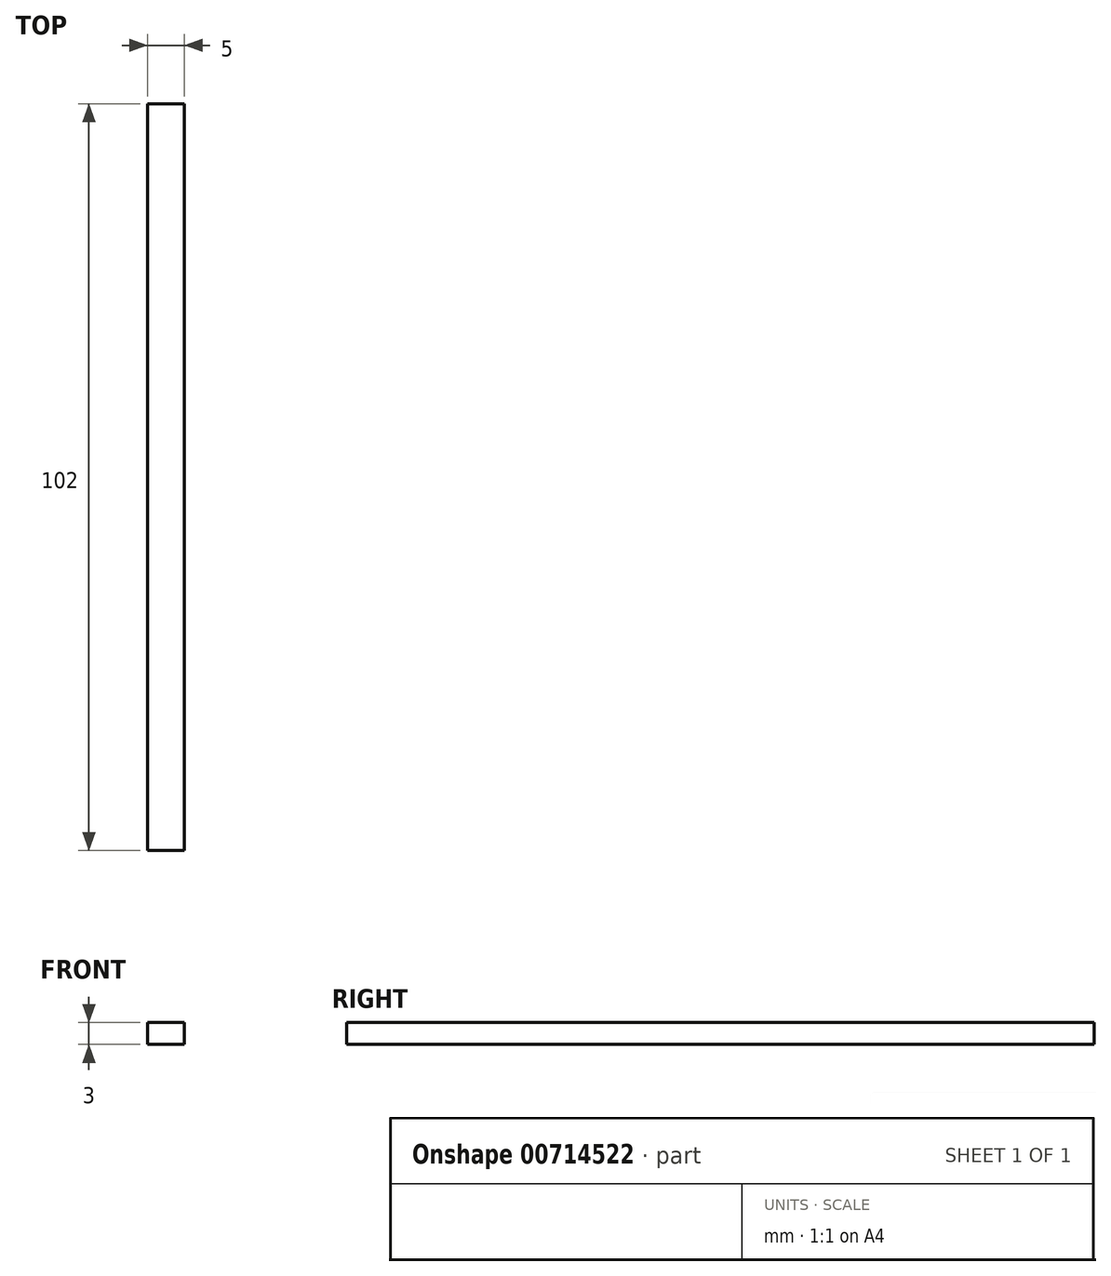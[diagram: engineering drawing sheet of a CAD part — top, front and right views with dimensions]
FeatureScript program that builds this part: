
annotation { "Feature Type Name" : "Feature", "Feature Type Description" : "" }
export const myFeature = defineFeature(function(context is Context, id is Id, definition is map)
    precondition{}
    {
        {
            var Q0;
            Q0=qCreatedBy(makeId("Right.planeOp"),FACE);
            var sketch = newSketch(context, id + "F0", { "sketchPlane" : qUnion([Q0])});
            skLineSegment(sketch, "E0.bottom", {"start": v(0, 0) * mm, "end": v(-102, 0) * mm});
            skLineSegment(sketch, "E0.top", {"start": v(0, 3) * mm, "end": v(-102, 3) * mm});
            skLineSegment(sketch, "E0.left", {"start": v(0, 0) * mm, "end": v(0, 3) * mm});
            skLineSegment(sketch, "E0.right", {"start": v(-102, 0) * mm, "end": v(-102, 3) * mm});
            skSolve(sketch);
        }
        {
            var Q0;
            Q0=makeQuery(id+"F0.imprint","IMPRINT",FACE,{"disambiguationData":[TD([[makeQuery(id+"F0.imprint","IMPRINT",EDGE,{"derivedFrom":sQuery(id+"F0.wireOp",EDGE,"E0.bottom")}),-1.0]])]});
            extrude(context, id + "F1", {"entities" : qUnion([Q0]), "depth" : 5 * mm, "offsetDistance" : 25 * mm});
        }
    });
